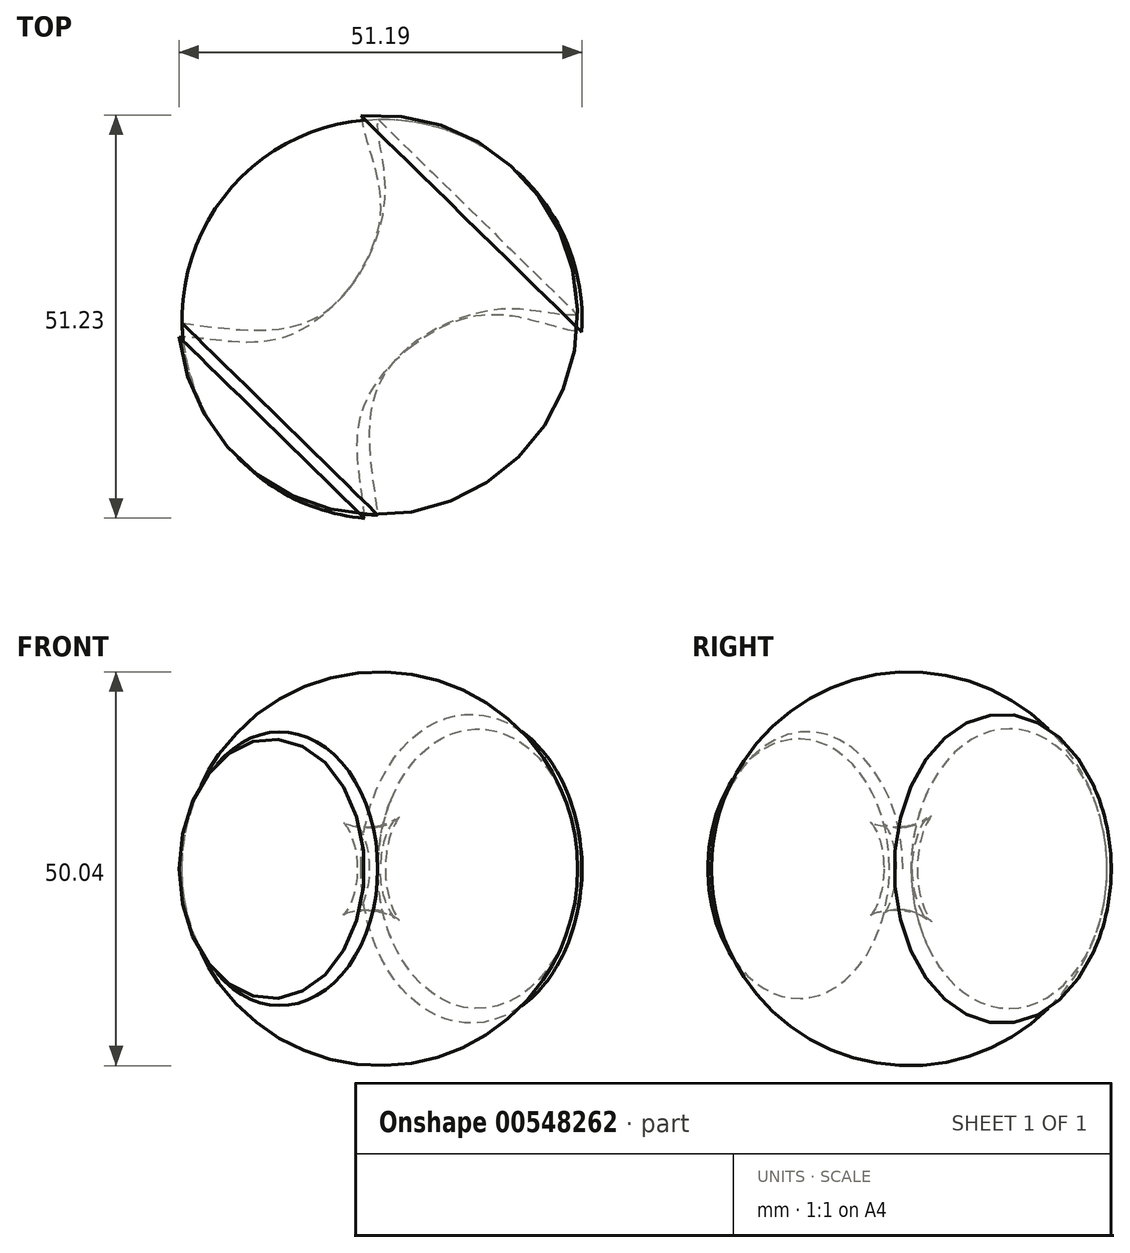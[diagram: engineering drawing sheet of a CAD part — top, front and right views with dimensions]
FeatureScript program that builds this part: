
annotation { "Feature Type Name" : "Feature", "Feature Type Description" : "" }
export const myFeature = defineFeature(function(context is Context, id is Id, definition is map)
    precondition{}
    {
        {
            var Q0;
            Q0=qCreatedBy(makeId("Top.planeOp"),FACE);
            var sketch = newSketch(context, id + "F0", { "sketchPlane" : qUnion([Q0])});
            skCircle(sketch, "E0", {"center": v(0, 0) * mm, "radius": 25.4 * mm});
            skLineSegment(sketch, "E1", {"start": v(18.04, 17.88) * mm, "end": v(-17.5, -18.41) * mm});
            skLineSegment(sketch, "E2", {"start": v(18, -17.91) * mm, "end": v(-18.28, 17.63) * mm});
            skFitSpline(sketch, "E3", {"points": [v(0, -25.4) * mm, v(0.58, -7.96) * mm, v(15.23, 0.7) * mm, v(25.4, 0) * mm], "startDerivative": vector(-7.37, 52.34) * mm, "endDerivative": vector(30.4, 2.74) * mm});
            skFitSpline(sketch, "E4", {"points": [v(-2.15, 25.3) * mm, v(0.22, 12.16) * mm, v(-11.17, -2.58) * mm, v(-25.25, -2.76) * mm], "startDerivative": vector(4.42, -34.62) * mm, "endDerivative": vector(-42.05, 1.3) * mm});
            skSolve(sketch);
        }
        {
            var Q0;
            {var subQ0=sQuery(id+"F0.wireOp",EDGE,"E1");var subQ1=sQuery(id+"F0.wireOp",EDGE,"E0");var subQ2=makeQuery(id+"F0.imprint","INTERSECT",VERTEX,{"disambiguationData":[OD(1.0)],"derivedFrom":[subQ1,subQ0]});Q0=makeQuery(id+"F0.imprint","IMPRINT",FACE,{"disambiguationData":[TD([[makeQuery(id+"F0.imprint","IMPRINT",EDGE,{"disambiguationData":[TD([[subQ2,-1.0]])],"derivedFrom":subQ1}),1.0]])]});}
            var Q1;
            {var subQ0=sQuery(id+"F0.wireOp",EDGE,"E2");var subQ1=sQuery(id+"F0.wireOp",EDGE,"E0");var subQ2=makeQuery(id+"F0.imprint","INTERSECT",VERTEX,{"disambiguationData":[OD(0.0)],"derivedFrom":[subQ1,subQ0]});Q1=makeQuery(id+"F0.imprint","IMPRINT",FACE,{"disambiguationData":[TD([[makeQuery(id+"F0.imprint","IMPRINT",EDGE,{"disambiguationData":[TD([[subQ2,1.0]])],"derivedFrom":subQ1}),1.0]])]});}
            var Q2;
            {var subQ0=sQuery(id+"F0.wireOp",EDGE,"E2");var subQ1=sQuery(id+"F0.wireOp",EDGE,"E0");var subQ2=makeQuery(id+"F0.imprint","INTERSECT",VERTEX,{"disambiguationData":[OD(0.0)],"derivedFrom":[subQ1,subQ0]});Q2=makeQuery(id+"F0.imprint","IMPRINT",FACE,{"disambiguationData":[TD([[makeQuery(id+"F0.imprint","IMPRINT",EDGE,{"disambiguationData":[TD([[subQ2,-1.0]])],"derivedFrom":subQ1}),1.0]])]});}
            var Q3;
            {var subQ0=sQuery(id+"F0.wireOp",EDGE,"E1");var subQ1=sQuery(id+"F0.wireOp",EDGE,"E0");var subQ2=makeQuery(id+"F0.imprint","INTERSECT",VERTEX,{"disambiguationData":[OD(0.0)],"derivedFrom":[subQ1,subQ0]});Q3=makeQuery(id+"F0.imprint","IMPRINT",FACE,{"disambiguationData":[TD([[makeQuery(id+"F0.imprint","IMPRINT",EDGE,{"disambiguationData":[TD([[subQ2,1.0]])],"derivedFrom":subQ1}),1.0]])]});}
            var Q4;
            Q4=sQuery(id+"F0.wireOp",EDGE,"E1");
            revolve(context, id + "F1", {"entities" : qUnion([Q0, Q1, Q2, Q3]), "axis" : qUnion([Q4]), "revolveType" : RevolveType.FULL});
        }
    });
